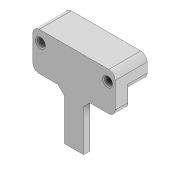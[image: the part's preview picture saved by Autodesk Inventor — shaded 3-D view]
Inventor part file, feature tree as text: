
AUTODESK INVENTOR PART (.ipt)
format: ipt  version: 2021 (Build 250183000, 183)  size: 168,960 bytes
history: native  units: mm
features: other x5, sketch x5, extrude x3, chamfer x3, reference x3, hole x2, projected_geometry x2, fillet x1
ambient origin geometry x8: Origin, YZ Plane, XZ Plane, XY Plane, X Axis, Y Axis, Z Axis, Center Point
bodies: Body1 (feature_tree)
feature tree (24):
  other  "Твердое тело1"
  other  "РабПлоскость1"
  extrude  "Выдавливание1"  Depth=5.0mm
  extrude  "Выдавливание2"  Depth=12.0mm
  fillet  "Сопряжение1"  Radius=2.0mm
  hole  "Отверстие1"  [1 undecoded]
  chamfer  "Фаска1"  Distance=2.0mm
  extrude  "Выдавливание3"  Depth=6.0mm TaperAngle=0.0deg
  chamfer  "Фаска2"  Distance=2.0mm
  hole  "Отверстие2"  [1 undecoded]
  chamfer  "Фаска3"  Distance=2.0mm Angle=45.0deg
  sketch  "Эскиз1"
  reference  "Ссылка1"
  reference  "Ссылка2"
  sketch  "Эскиз2"
  reference  "Ссылка3"
  projected_geometry  "Спроецированная петля1"
  sketch  "Эскиз3"
  projected_geometry  "Спроецированная петля2"
  sketch  "Эскиз4"
  sketch  "Эскиз5"
  other  "<userpath>\Desktop\теплица\датчики почва воздух\Компоновка.iam"
  other  "Компоновка.iam"
  other  "Wemos_D1_mini:1"
note: 2 required parameter values undecoded (feature->parameter linkage not recoverable at this tier; creation-order binding heuristic only, values carry confidence <= 0.55)
